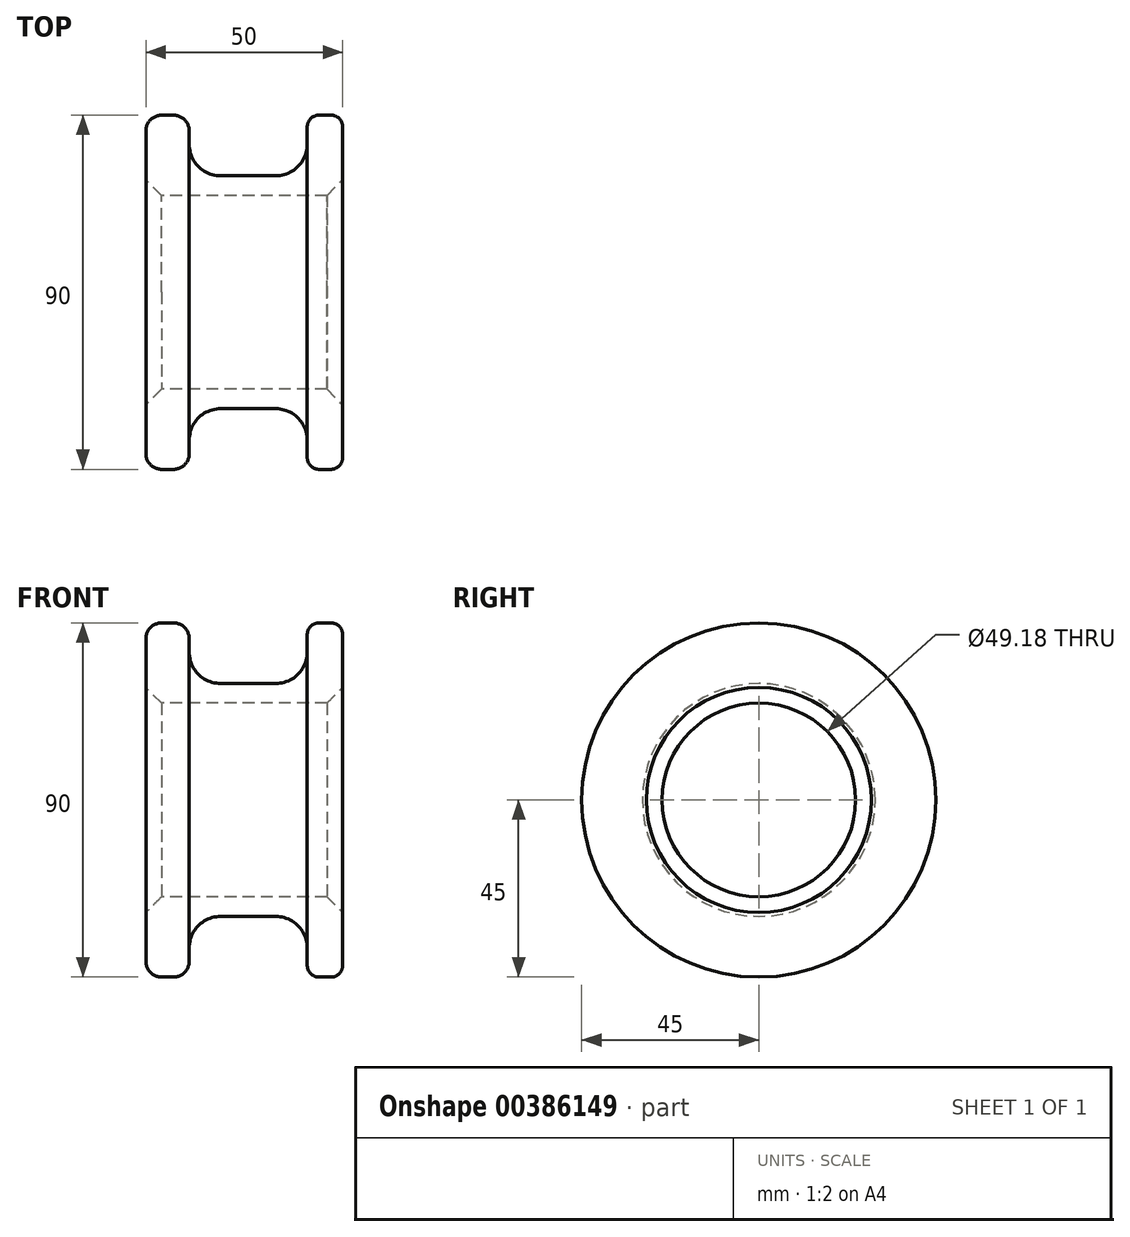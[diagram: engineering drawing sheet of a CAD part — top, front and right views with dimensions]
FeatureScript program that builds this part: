
annotation { "Feature Type Name" : "Feature", "Feature Type Description" : "" }
export const myFeature = defineFeature(function(context is Context, id is Id, definition is map)
    precondition{}
    {
        {
            var Q0;
            Q0=qCreatedBy(makeId("Front.planeOp"),FACE);
            var sketch = newSketch(context, id + "F0", { "sketchPlane" : qUnion([Q0])});
            skLineSegment(sketch, "E0", {"start": v(0, 41) * mm, "end": v(0, 24.59) * mm});
            skLineSegment(sketch, "E1", {"start": v(0, 24.59) * mm, "end": v(50, 24.59) * mm});
            skLineSegment(sketch, "E2", {"start": v(50, 24.59) * mm, "end": v(50, 42) * mm});
            skLineSegment(sketch, "E3", {"start": v(47, 45) * mm, "end": v(44, 45) * mm});
            skLineSegment(sketch, "E4", {"start": v(41, 42) * mm, "end": v(41, 37.59) * mm});
            skLineSegment(sketch, "E5", {"start": v(33, 29.59) * mm, "end": v(19, 29.59) * mm});
            skLineSegment(sketch, "E6", {"start": v(11, 37.59) * mm, "end": v(11, 41) * mm});
            skLineSegment(sketch, "E7", {"start": v(7, 45) * mm, "end": v(4, 45) * mm});
            skPoint(sketch, "E8.visualSharp", {"position": v(11, 29.59) * mm});
            skArc(sketch, "E8.filletArc", {"start": v(11, 37.59) * mm, "mid": v(13.34, 31.93) * mm, "end": v(19, 29.59) * mm});
            skPoint(sketch, "E9.visualSharp", {"position": v(41, 29.59) * mm});
            skArc(sketch, "E9.filletArc", {"start": v(33, 29.59) * mm, "mid": v(38.66, 31.93) * mm, "end": v(41, 37.59) * mm});
            skPoint(sketch, "E10.visualSharp", {"position": v(11, 45) * mm});
            skArc(sketch, "E10.filletArc", {"start": v(11, 41) * mm, "mid": v(9.83, 43.83) * mm, "end": v(7, 45) * mm});
            skPoint(sketch, "E11.visualSharp", {"position": v(41, 45) * mm});
            skArc(sketch, "E11.filletArc", {"start": v(44, 45) * mm, "mid": v(41.88, 44.12) * mm, "end": v(41, 42) * mm});
            skPoint(sketch, "E12.visualSharp", {"position": v(50, 45) * mm});
            skArc(sketch, "E12.filletArc", {"start": v(50, 42) * mm, "mid": v(49.12, 44.12) * mm, "end": v(47, 45) * mm});
            skPoint(sketch, "E13.visualSharp", {"position": v(0, 45) * mm});
            skArc(sketch, "E13.filletArc", {"start": v(4, 45) * mm, "mid": v(1.17, 43.83) * mm, "end": v(0, 41) * mm});
            skLineSegment(sketch, "E14", {"start": v(0, 0) * mm, "end": v(77.35, 0) * mm});
            skSolve(sketch);
        }
        {
            var Q0;
            Q0=makeQuery(id+"F0.imprint","IMPRINT",FACE,{"disambiguationData":[TD([[makeQuery(id+"F0.imprint","IMPRINT",EDGE,{"derivedFrom":sQuery(id+"F0.wireOp",EDGE,"E0")}),1.0]])]});
            var Q1;
            Q1=sQuery(id+"F0.wireOp",EDGE,"E14");
            revolve(context, id + "F1", {"entities" : qUnion([Q0]), "axis" : qUnion([Q1]), "revolveType" : RevolveType.FULL});
        }
        {
            var Q0;
            Q0=makeQuery(id+"F1.opRevolve","SWEPT_FACE",FACE,{"disambiguationData":[OSD([sQuery(id+"F0.wireOp",EDGE,"E1")])]});
            chamfer(context, id + "F2", {"entities" : qUnion([Q0]), "width" : 4 * mm, "tangentPropagation" : true});
        }
    });
